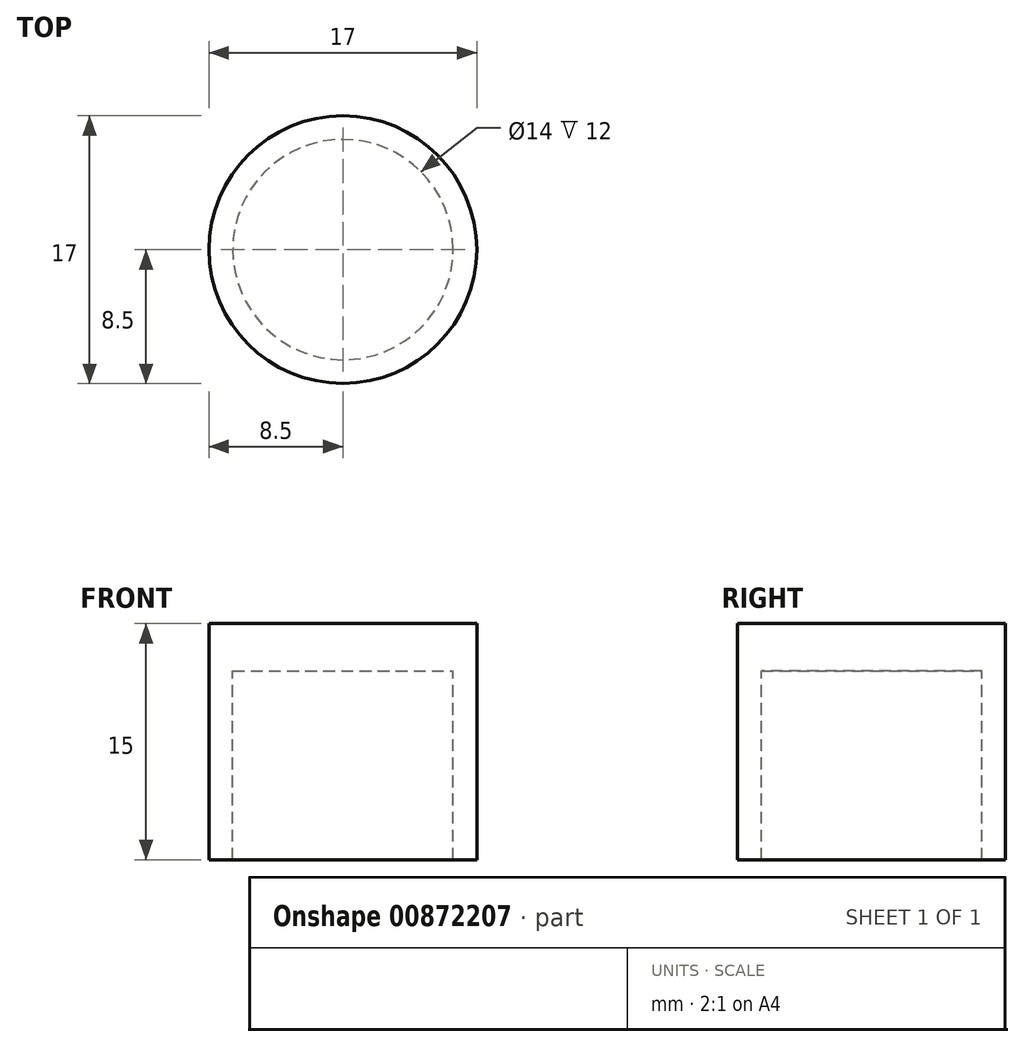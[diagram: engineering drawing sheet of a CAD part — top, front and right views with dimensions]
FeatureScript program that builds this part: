
annotation { "Feature Type Name" : "Feature", "Feature Type Description" : "" }
export const myFeature = defineFeature(function(context is Context, id is Id, definition is map)
    precondition{}
    {
        {
            var Q0;
            Q0=qCreatedBy(makeId("Top.planeOp"),FACE);
            var sketch = newSketch(context, id + "F0", { "sketchPlane" : qUnion([Q0])});
            skCircle(sketch, "E0", {"center": v(0, 0) * mm, "radius": 8.5 * mm});
            skSolve(sketch);
        }
        {
            var Q0;
            Q0 = qSketchRegion(id + "F0", true);
            extrude(context, id + "F1", {"entities" : qUnion([Q0]), "depth" : 3 * mm, "offsetDistance" : 25.4 * mm});
        }
        {
            var Q0;
            Q0=makeQuery(id+"F1.opExtrude","CAP_FACE",FACE,{"disambiguationData":[OSD([sQuery(id+"F0.wireOp",EDGE,"E0")])],"isStart":true});
            var sketch = newSketch(context, id + "F2", { "sketchPlane" : qUnion([Q0])});
            skCircle(sketch, "E1", {"center": v(0, 0) * mm, "radius": 7 * mm});
            skSolve(sketch);
        }
        {
            var Q0;
            Q0=makeQuery(id+"F2.imprint","IMPRINT",FACE,{"disambiguationData":[TD([[makeQuery(id+"F2.imprint","IMPRINT",EDGE,{"derivedFrom":sQuery(id+"F2.wireOp",EDGE,"E1")}),-1.0]])]});
            extrude(context, id + "F3", {"entities" : qUnion([Q0]), "operationType" : NewBodyOperationType.ADD, "depth" : 12 * mm, "offsetDistance" : 25.4 * mm});
        }
    });
